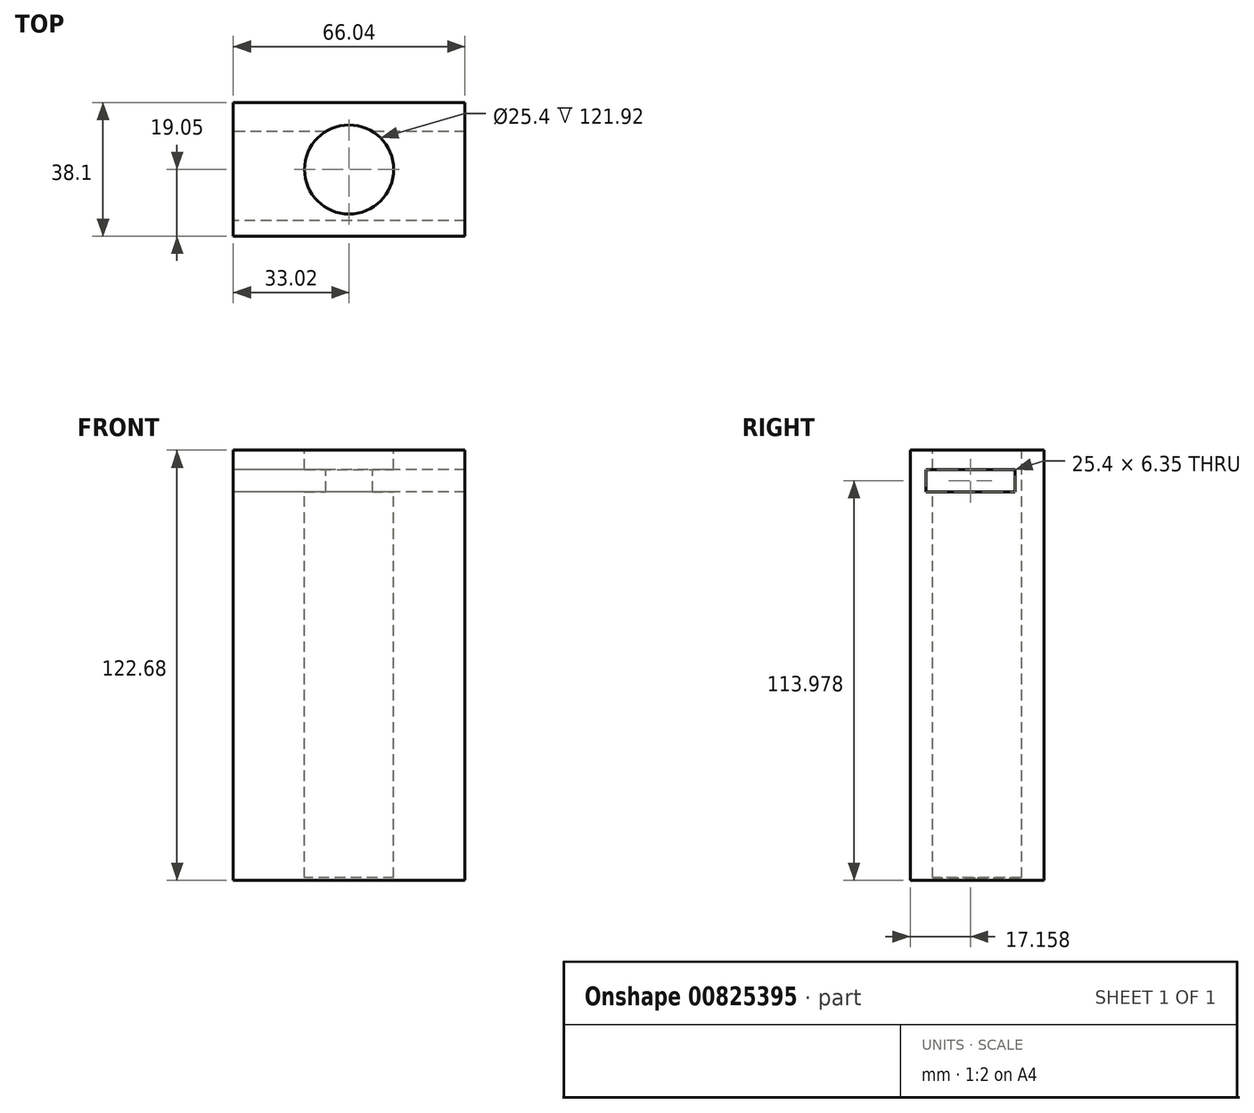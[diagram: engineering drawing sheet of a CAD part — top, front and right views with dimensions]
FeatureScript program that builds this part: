
annotation { "Feature Type Name" : "Feature", "Feature Type Description" : "" }
export const myFeature = defineFeature(function(context is Context, id is Id, definition is map)
    precondition{}
    {
        {
            var Q0;
            Q0=qCreatedBy(makeId("Front.planeOp"),FACE);
            var sketch = newSketch(context, id + "F0", { "sketchPlane" : qUnion([Q0])});
            skLineSegment(sketch, "E0", {"start": v(0, -55) * mm, "end": v(0, 67.68) * mm});
            skLineSegment(sketch, "E1", {"start": v(0, -55) * mm, "end": v(66.04, -55) * mm});
            skLineSegment(sketch, "E2", {"start": v(66.04, -55) * mm, "end": v(66.04, 67.68) * mm});
            skLineSegment(sketch, "E3", {"start": v(0, 67.68) * mm, "end": v(66.04, 67.68) * mm});
            skSolve(sketch);
        }
        {
            var Q0;
            Q0=qSketchRegion(id+"F0",true);
            extrude(context, id + "F1", {"entities" : qUnion([Q0]), "depth" : 38.1 * mm, "offsetDistance" : 25.4 * mm});
        }
        {
            var Q0;
            Q0=makeQuery(id+"F1.opExtrude","SWEPT_FACE",FACE,{"disambiguationData":[OSD([sQuery(id+"F0.wireOp",EDGE,"E3")])]});
            var sketch = newSketch(context, id + "F2", { "sketchPlane" : qUnion([Q0])});
            skCircle(sketch, "E4", {"center": v(33.02, -19.05) * mm, "radius": 12.7 * mm});
            skSolve(sketch);
        }
        {
            var Q0;
            Q0=qCreatedBy(makeId("Right.planeOp"),FACE);
            var sketch = newSketch(context, id + "F3", { "sketchPlane" : qUnion([Q0])});
            skLineSegment(sketch, "E5", {"start": v(-33.64, 62.15) * mm, "end": v(-8.24, 62.15) * mm});
            skLineSegment(sketch, "E6", {"start": v(-8.24, 62.15) * mm, "end": v(-8.24, 55.8) * mm});
            skLineSegment(sketch, "E7", {"start": v(-8.24, 55.8) * mm, "end": v(-33.64, 55.8) * mm});
            skLineSegment(sketch, "E8", {"start": v(-33.64, 55.8) * mm, "end": v(-33.64, 62.15) * mm});
            skSolve(sketch);
        }
        {
            var Q0;
            Q0=qSketchRegion(id+"F3",true);
            extrude(context, id + "F4", {"entities" : qUnion([Q0]), "operationType" : NewBodyOperationType.REMOVE, "depth" : 66.04 * mm, "offsetDistance" : 25.4 * mm});
        }
        {
            var Q0;
            Q0=qSketchRegion(id+"F2",true);
            extrude(context, id + "F5", {"entities" : qUnion([Q0]), "operationType" : NewBodyOperationType.REMOVE, "oppositeDirection" : true, "depth" : 121.92 * mm, "offsetDistance" : 25.4 * mm});
        }
    });
